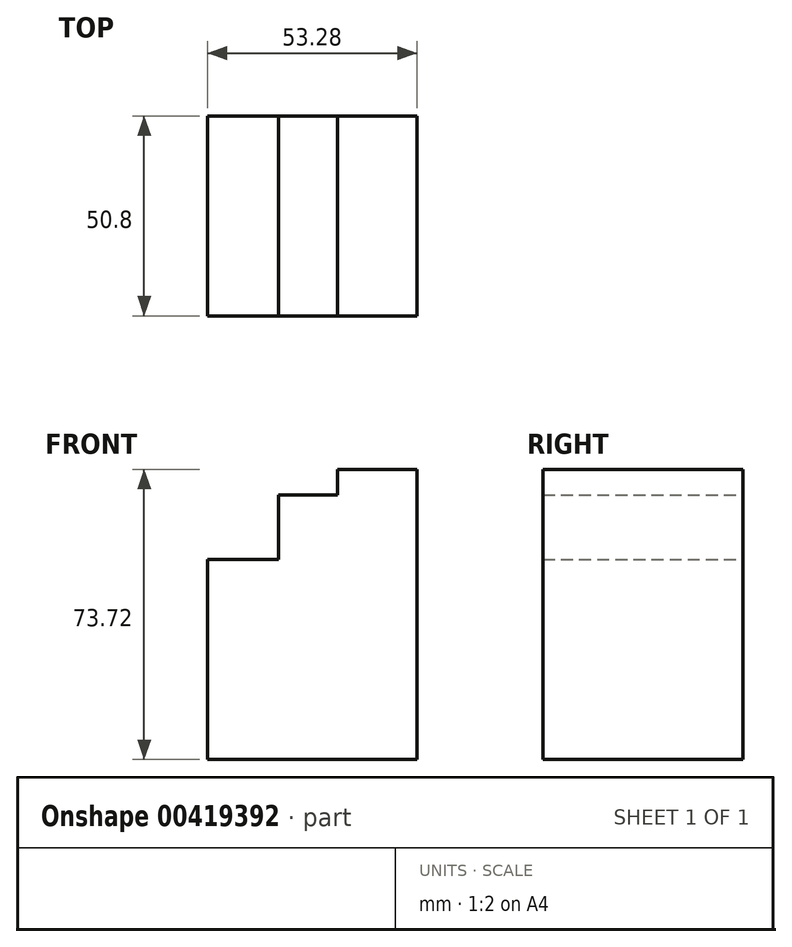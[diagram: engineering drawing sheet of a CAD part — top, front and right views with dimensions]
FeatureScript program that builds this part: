
annotation { "Feature Type Name" : "Feature", "Feature Type Description" : "" }
export const myFeature = defineFeature(function(context is Context, id is Id, definition is map)
    precondition{}
    {
        {
            var Q0;
            Q0=qCreatedBy(makeId("Front.planeOp"),FACE);
            var sketch = newSketch(context, id + "F0", { "sketchPlane" : qUnion([Q0])});
            skLineSegment(sketch, "E0", {"start": v(0, 0) * mm, "end": v(0, 76.2) * mm});
            skLineSegment(sketch, "E1", {"start": v(0, 76.2) * mm, "end": v(-20.24, 76.2) * mm});
            skLineSegment(sketch, "E2", {"start": v(-20.24, 76.2) * mm, "end": v(-20.24, 69.7) * mm});
            skLineSegment(sketch, "E3", {"start": v(-20.24, 69.7) * mm, "end": v(-35.14, 69.7) * mm});
            skLineSegment(sketch, "E4", {"start": v(-35.14, 69.7) * mm, "end": v(-35.14, 53.28) * mm});
            skLineSegment(sketch, "E5", {"start": v(-35.14, 53.28) * mm, "end": v(-53.28, 53.28) * mm});
            skLineSegment(sketch, "E6", {"start": v(-53.28, 53.28) * mm, "end": v(-53.28, 2.48) * mm});
            skLineSegment(sketch, "E7", {"start": v(-53.28, 2.48) * mm, "end": v(-2.48, 2.48) * mm});
            skLineSegment(sketch, "E8", {"start": v(-2.48, 2.48) * mm, "end": v(0, 2.48) * mm});
            skSolve(sketch);
        }
        {
            var Q0;
            Q0 = qSketchRegion(id + "F0", true);
            extrude(context, id + "F1", {"entities" : qUnion([Q0]), "depth" : 25.4 * mm});
        }
        {
            var Q0;
            Q0 = qSketchRegion(id + "F0", true);
            extrude(context, id + "F2", {"entities" : qUnion([Q0]), "operationType" : NewBodyOperationType.ADD, "depth" : 50.8 * mm});
        }
    });
